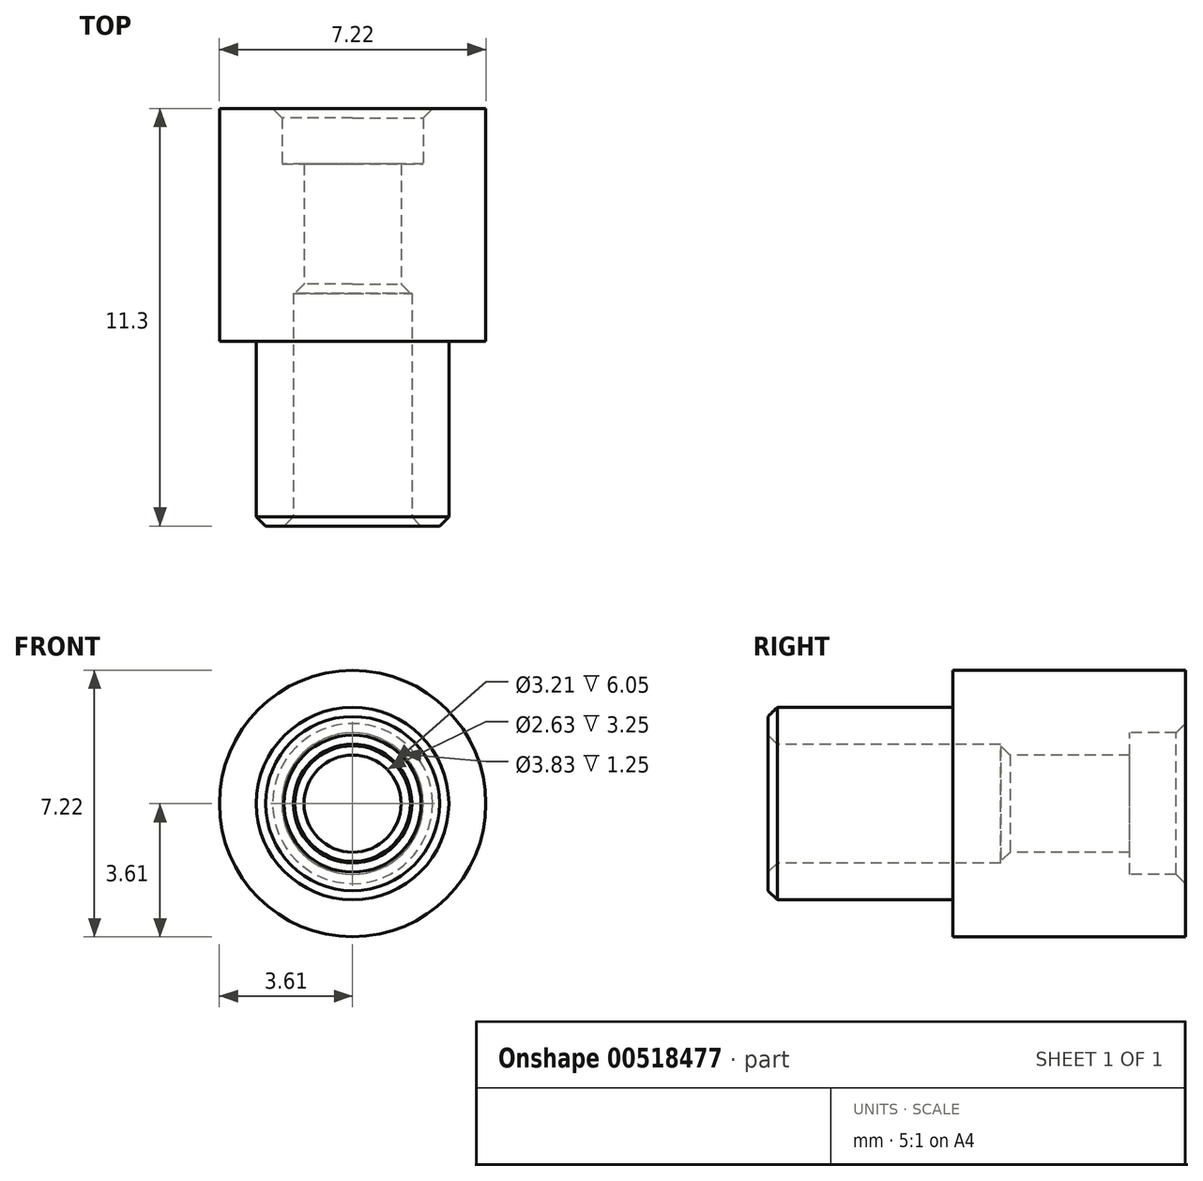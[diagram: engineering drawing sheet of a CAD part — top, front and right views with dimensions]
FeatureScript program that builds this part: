
annotation { "Feature Type Name" : "Feature", "Feature Type Description" : "" }
export const myFeature = defineFeature(function(context is Context, id is Id, definition is map)
    precondition{}
    {
        {
            var Q0;
            Q0=qCreatedBy(makeId("Right.planeOp"),FACE);
            var sketch = newSketch(context, id + "F0", { "sketchPlane" : qUnion([Q0])});
            skLineSegment(sketch, "E0", {"start": v(-7.9, 2.6) * mm, "end": v(-7.9, 1.6) * mm});
            skLineSegment(sketch, "E1", {"start": v(-7.9, 1.6) * mm, "end": v(-1.6, 1.6) * mm});
            skLineSegment(sketch, "E2", {"start": v(-1.6, 1.6) * mm, "end": v(-1.6, 1.31) * mm});
            skLineSegment(sketch, "E3", {"start": v(-1.6, 1.31) * mm, "end": v(1.9, 1.31) * mm});
            skLineSegment(sketch, "E4", {"start": v(1.9, 1.31) * mm, "end": v(1.9, 1.92) * mm});
            skLineSegment(sketch, "E5", {"start": v(1.9, 1.92) * mm, "end": v(3.4, 1.92) * mm});
            skLineSegment(sketch, "E6", {"start": v(-7.9, 2.6) * mm, "end": v(-2.9, 2.6) * mm});
            skLineSegment(sketch, "E7", {"start": v(-2.9, 2.6) * mm, "end": v(-2.9, 3.6) * mm});
            skLineSegment(sketch, "E8", {"start": v(-2.9, 3.6) * mm, "end": v(3.4, 3.6) * mm});
            skLineSegment(sketch, "E9", {"start": v(3.4, 3.6) * mm, "end": v(3.4, 1.91) * mm});
            skLineSegment(sketch, "E10", {"start": v(-5.4, 0) * mm, "end": v(6.88, 0) * mm, "construction": true});
            skLineSegment(sketch, "E11.MirrorCS", {"start": v(-1.6, -1.31) * mm, "end": v(1.9, -1.31) * mm, "construction": true});
            skLineSegment(sketch, "E12.MirrorCS", {"start": v(-7.9, -1.6) * mm, "end": v(-1.6, -1.6) * mm, "construction": true});
            skLineSegment(sketch, "E13.MirrorCS", {"start": v(1.9, -1.92) * mm, "end": v(3.4, -1.92) * mm, "construction": true});
            skLineSegment(sketch, "E14.MirrorCS", {"start": v(-7.9, -2.6) * mm, "end": v(-2.9, -2.6) * mm, "construction": true});
            skLineSegment(sketch, "E15.MirrorCS", {"start": v(-2.9, -3.6) * mm, "end": v(3.4, -3.6) * mm, "construction": true});
            skCircle(sketch, "E16", {"center": v(-2.56, 0) * mm, "radius": 1.6 * mm, "construction": true});
            skLineSegment(sketch, "E17.bottom", {"start": v(1.9, 1.3) * mm, "end": v(-0.44, 1.3) * mm, "construction": true});
            skLineSegment(sketch, "E17.top", {"start": v(1.9, -1.3) * mm, "end": v(-0.44, -1.3) * mm, "construction": true});
            skLineSegment(sketch, "E17.left", {"start": v(1.9, 1.3) * mm, "end": v(1.9, -1.3) * mm, "construction": true});
            skLineSegment(sketch, "E17.right", {"start": v(-0.44, 1.3) * mm, "end": v(-0.44, -1.3) * mm, "construction": true});
            skPoint(sketch, "E17.middle", {"position": v(0.73, 0) * mm});
            skPoint(sketch, "E18", {"position": v(0.4, 0) * mm});
            skSolve(sketch);
        }
        {
            var Q0;
            Q0 = qSketchRegion(id + "F0", true);
            var Q1;
            Q1=sQuery(id+"F0.wireOp",EDGE,"E10");
            revolve(context, id + "F1", {"entities" : qUnion([Q0]), "axis" : qUnion([Q1]), "revolveType" : RevolveType.FULL});
        }
        {
            var Q0;
            Q0=makeQuery(id+"F1.opRevolve","SWEPT_EDGE",EDGE,{"disambiguationData":[OSD([sQuery(id+"F0.wireOp",EDGE,"E5"),sQuery(id+"F0.wireOp",EDGE,"E9")])]});
            var Q1;
            Q1=makeQuery(id+"F1.opRevolve","SWEPT_EDGE",EDGE,{"disambiguationData":[OSD([sQuery(id+"F0.wireOp",EDGE,"E0"),sQuery(id+"F0.wireOp",EDGE,"E1")])]});
            var Q2;
            Q2=makeQuery(id+"F1.opRevolve","SWEPT_EDGE",EDGE,{"disambiguationData":[OSD([sQuery(id+"F0.wireOp",EDGE,"E0"),sQuery(id+"F0.wireOp",EDGE,"E6")])]});
            var Q3;
            Q3=makeQuery(id+"F1.opRevolve","SWEPT_EDGE",EDGE,{"disambiguationData":[OSD([sQuery(id+"F0.wireOp",EDGE,"E2"),sQuery(id+"F0.wireOp",EDGE,"E3")])]});
            chamfer(context, id + "F2", {"entities" : qUnion([Q0, Q1, Q2, Q3]), "width" : .25 * mm, "tangentPropagation" : true});
        }
    });
